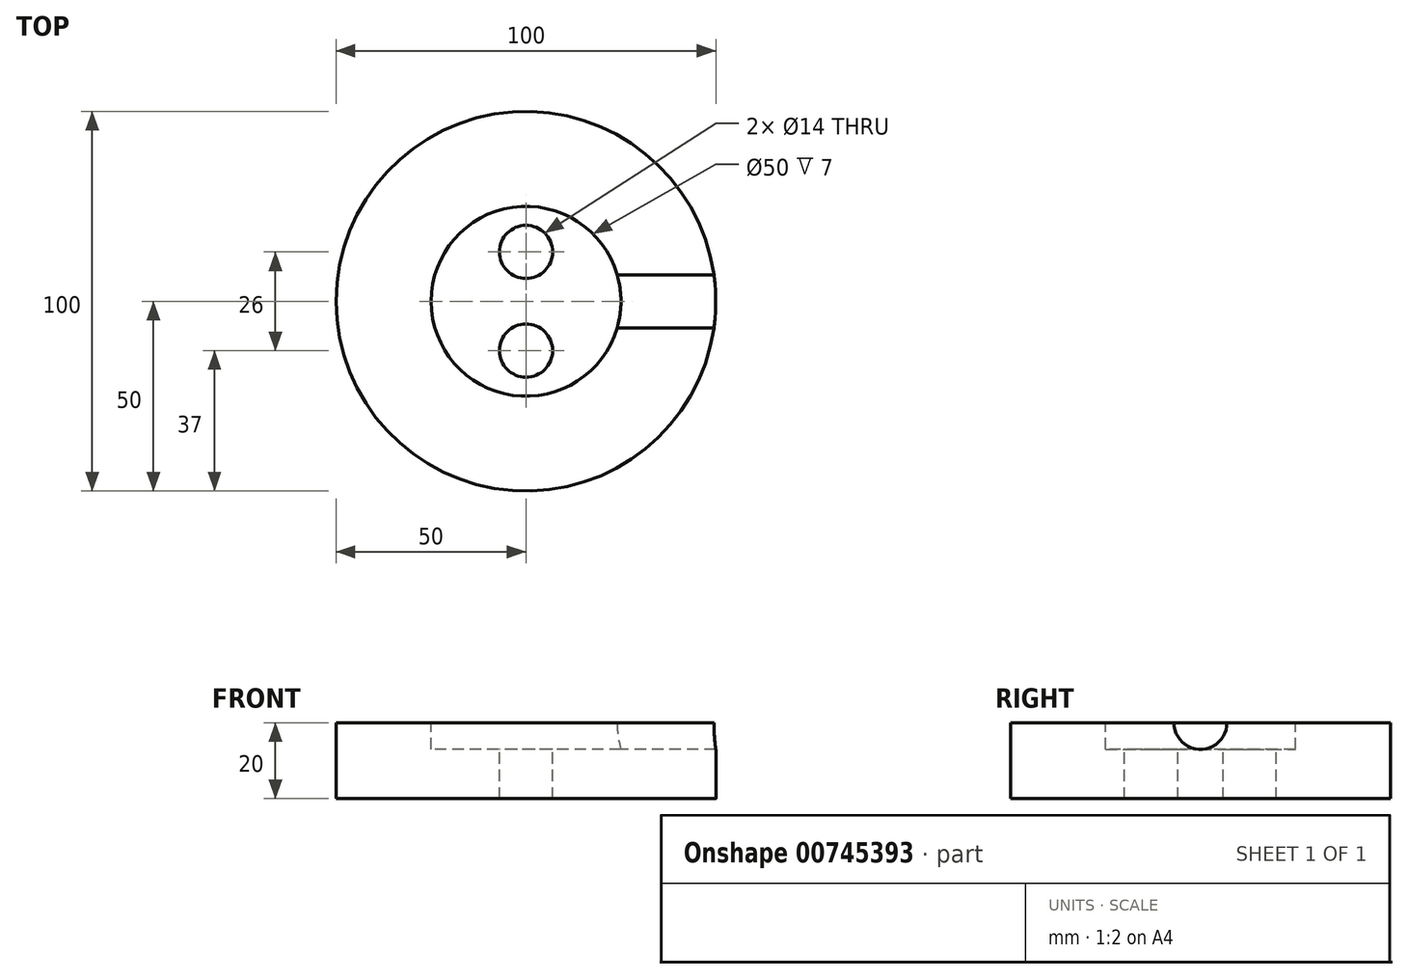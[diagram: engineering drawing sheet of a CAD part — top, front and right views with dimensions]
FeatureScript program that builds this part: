
annotation { "Feature Type Name" : "Feature", "Feature Type Description" : "" }
export const myFeature = defineFeature(function(context is Context, id is Id, definition is map)
    precondition{}
    {
        {
            var Q0;
            Q0=qCreatedBy(makeId("Top.planeOp"),FACE);
            var sketch = newSketch(context, id + "F0", { "sketchPlane" : qUnion([Q0])});
            skCircle(sketch, "E0", {"center": v(0, 0) * mm, "radius": 50 * mm});
            skSolve(sketch);
        }
        {
            var Q0;
            Q0 = qSketchRegion(id + "F0", true);
            extrude(context, id + "F1", {"entities" : qUnion([Q0]), "depth" : 20 * mm, "offsetDistance" : 25 * mm});
        }
        {
            var Q0;
            Q0=makeQuery(id+"F1.opExtrude","CAP_FACE",FACE,{"disambiguationData":[OSD([sQuery(id+"F0.wireOp",EDGE,"E0")])],"isStart":false});
            var sketch = newSketch(context, id + "F2", { "sketchPlane" : qUnion([Q0])});
            skCircle(sketch, "E1", {"center": v(0, 0) * mm, "radius": 25 * mm});
            skSolve(sketch);
        }
        {
            var Q0;
            Q0 = qSketchRegion(id + "F2", true);
            extrude(context, id + "F3", {"entities" : qUnion([Q0]), "operationType" : NewBodyOperationType.REMOVE, "oppositeDirection" : true, "depth" : 7 * mm, "offsetDistance" : 25 * mm});
        }
        {
            var Q0;
            Q0=qCreatedBy(makeId("Right.planeOp"),FACE);
            var sketch = newSketch(context, id + "F4", { "sketchPlane" : qUnion([Q0])});
            skCircle(sketch, "E2", {"center": v(0, 20) * mm, "radius": 7 * mm});
            skSolve(sketch);
        }
        {
            var Q0;
            Q0 = qSketchRegion(id + "F4", true);
            extrude(context, id + "F5", {"entities" : qUnion([Q0]), "operationType" : NewBodyOperationType.REMOVE, "endBound" : BoundingType.THROUGH_ALL, "depth" : 25 * mm, "offsetDistance" : 25 * mm});
        }
        {
            var Q0;
            Q0=makeQuery(id+"F3.boolean.opBoolean","COPY",FACE,{"derivedFrom":makeQuery(id+"F3.opExtrude","CAP_FACE",FACE,{"disambiguationData":[OSD([sQuery(id+"F2.wireOp",EDGE,"E1")])],"isStart":false})});
            var sketch = newSketch(context, id + "F6", { "sketchPlane" : qUnion([Q0])});
            skCircle(sketch, "E3", {"center": v(0, 13) * mm, "radius": 7 * mm});
            skCircle(sketch, "E4", {"center": v(0, -13) * mm, "radius": 7 * mm});
            skSolve(sketch);
        }
        {
            var Q0;
            Q0 = qSketchRegion(id + "F6", true);
            extrude(context, id + "F7", {"entities" : qUnion([Q0]), "operationType" : NewBodyOperationType.REMOVE, "oppositeDirection" : true, "depth" : 20 * mm, "offsetDistance" : 25 * mm});
        }
    });
